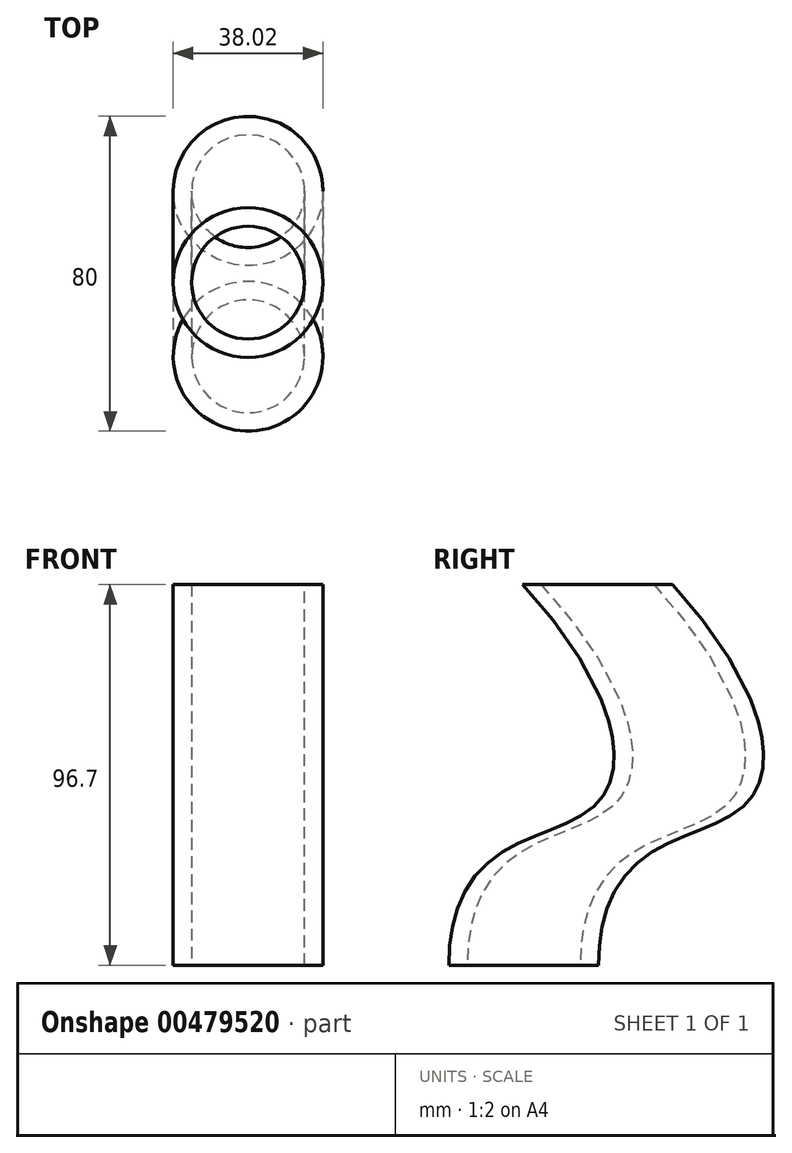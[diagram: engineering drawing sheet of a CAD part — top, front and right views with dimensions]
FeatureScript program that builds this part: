
annotation { "Feature Type Name" : "Feature", "Feature Type Description" : "" }
export const myFeature = defineFeature(function(context is Context, id is Id, definition is map)
    precondition{}
    {
        {
            var Q0;
            Q0=qCreatedBy(makeId("Top.planeOp"),FACE);
            var sketch = newSketch(context, id + "F0", { "sketchPlane" : qUnion([Q0])});
            skCircle(sketch, "E0", {"center": v(0, 0) * mm, "radius": 19.01 * mm});
            skCircle(sketch, "E1", {"center": v(0, 0) * mm, "radius": 14.32 * mm});
            skSolve(sketch);
        }
        {
            var Q0;
            Q0=qCreatedBy(makeId("Right.planeOp"),FACE);
            var sketch = newSketch(context, id + "F1", { "sketchPlane" : qUnion([Q0])});
            skFitSpline(sketch, "E2", {"points": [v(0, 0) * mm, v(36.57, 40.08) * mm, v(18.72, 96.7) * mm], "startDerivative": vector(0, 205.47) * mm, "endDerivative": vector(-135.12, 144.97) * mm});
            skSolve(sketch);
        }
        {
            var Q0;
            Q0 = qSketchRegion(id + "F0", true);
            var Q1;
            Q1 = qConstructionFilter(qBodyType(qCreatedBy(id + "F1" ,EDGE), BodyType.WIRE), ConstructionObject.NO);
            sweep(context, id + "F2", {"profiles" : qUnion([Q0]), "path" : qUnion([Q1]), "keepProfileOrientation" : true});
        }
    });
